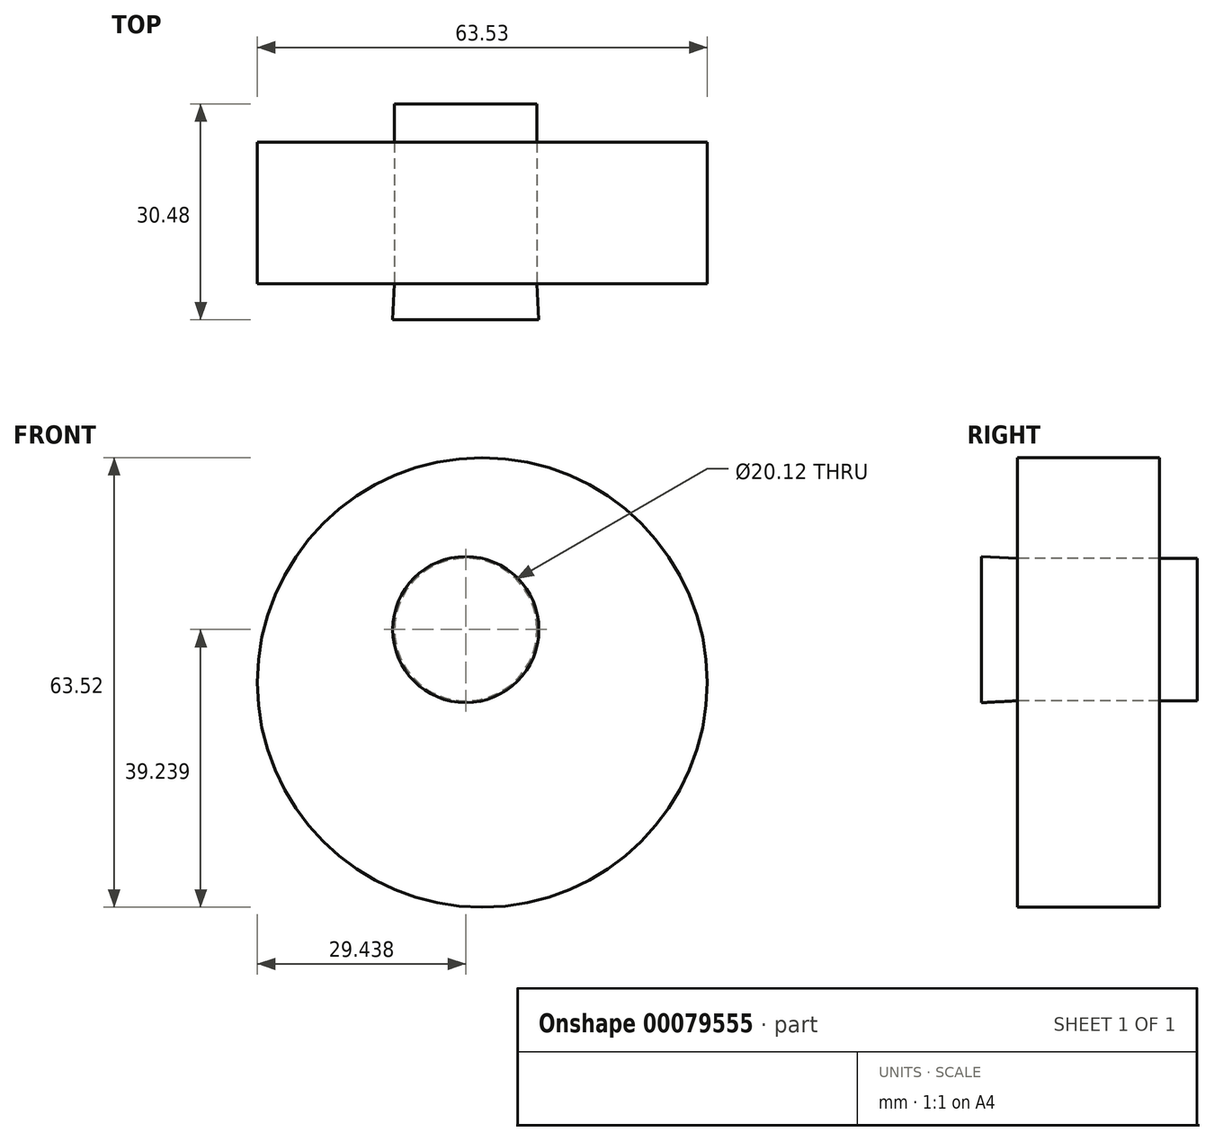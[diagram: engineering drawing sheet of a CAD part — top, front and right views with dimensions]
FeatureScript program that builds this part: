
annotation { "Feature Type Name" : "Feature", "Feature Type Description" : "" }
export const myFeature = defineFeature(function(context is Context, id is Id, definition is map)
    precondition{}
    {
        {
            var Q0;
            Q0=qCreatedBy(makeId("Front.planeOp"),FACE);
            var sketch = newSketch(context, id + "F0", { "sketchPlane" : qUnion([Q0])});
            skCircle(sketch, "E0", {"center": v(-12.46, 26.42) * mm, "radius": 10.06 * mm});
            skCircle(sketch, "E1", {"center": v(-10.14, 18.94) * mm, "radius": 31.76 * mm});
            skSolve(sketch);
        }
        {
            var Q0;
            Q0=makeQuery(id+"F0.imprint","IMPRINT",FACE,{"disambiguationData":[TD([[makeQuery(id+"F0.imprint","IMPRINT",EDGE,{"derivedFrom":sQuery(id+"F0.wireOp",EDGE,"E0")}),-1.0]])]});
            extrude(context, id + "F1", {"entities" : qUnion([Q0]), "oppositeDirection" : true, "depth" : 20.03 * mm});
        }
        {
            var Q0;
            Q0=makeQuery(id+"F1.opExtrude","CAP_FACE",FACE,{"disambiguationData":[OSD([sQuery(id+"F0.wireOp",EDGE,"E0"),sQuery(id+"F0.wireOp",EDGE,"E1")])],"isStart":true});
            var sketch = newSketch(context, id + "F2", { "sketchPlane" : qUnion([Q0])});
            skSolve(sketch);
        }
        {
            var Q0;
            Q0=makeQuery(id+"F2.imprint","IMPRINT",FACE,{"disambiguationData":[TD([[makeQuery(id+"F2.imprint","IMPRINT",EDGE,{"derivedFrom":makeQuery(id+"F1.opExtrude","CAP_EDGE",EDGE,{"disambiguationData":[OSD([sQuery(id+"F0.wireOp",EDGE,"E0")])],"isStart":true})}),1.0]])]});
            extrude(context, id + "F3", {"entities" : qUnion([Q0]), "depth" : 5.08 * mm, "hasDraft" : true, "draftAngle" : 3 * degree});
        }
        {
            var Q0;
            Q0=makeQuery(id+"F3.opExtrude","CAP_FACE",FACE,{"disambiguationData":[OSD([sQuery(id+"F0.wireOp",EDGE,"E0")])],"isStart":true});
            extrude(context, id + "F4", {"entities" : qUnion([Q0]), "depth" : 25.4 * mm});
        }
    });
